# Revit family: ALBA_R100ExSWxxS
name_source: partatom
category: Leuchten
units: mm (PartAtom-declared; Revit-internal decimal feet)

## family parameters
Basisbauteil = Fläche
Beim Laden mit Abzugskörper schneiden = Nein
Bemaßung runder Anschluss = Durchmesser verwenden
Gemeinsam genutzt = Nein
Lichtquelle = Ja
OmniClass-Nummer = 23.80.70.11
OmniClass-Titel = Luminaries for Internal Lighting
Raumberechnungspunkt = Nein
Teiletyp = Normal

## types (8) — shared parameters
Baugruppenkennzeichen = D5020200
Datei für fotometrisches Netz = Master_ALBA_R100E_SW_Linse_S.IES
Emissionsform beim Rendern sichtbar = Nein
Farbfilter = 16777215
Farbtemperaturverschiebung bei Dämpfen der Lampe = <Keine Auswahl>
Hersteller = RIDI Leuchten GmbH
Lampe = LED
Neigungswinkel = 90.00°
Scheinlast = 15 VA
URL = www.ridi.de
Von Kreisdurchmesser aussenden = 86 mm  [stored 0.282152 ft]
brand = RIDI
conformity mark = CE
electrical safety class = 2
height = 84 mm  [stored 0.275591 ft]
ingress protection (IP) code = IP20
length = 112 mm  [stored 0.367454 ft]
nominal frequency = 50-60Hz
nominal voltage = 230
rated input power = 15
voltage type (AC, DC, UC) = AC
weight = 0.43 kg
width = 112 mm  [stored 0.367454 ft]
zero-valued in all types: Vorgabe-Ansicht

## per-type parameters (varying)
| type | Modell |
| ALBA R100E NDSW840S0200 | 0322319 |
| ALBA R100E NDSW830S0200 | 0322318 |
| ALBA R100E NDSW930S0175 | 0322320 |
| ALBA R100E NDSW940S0175 | 0322321 |
| ALBA R100E DASW830S0200 | 0332318 |
| ALBA R100E DASW840S0200 | 0332319 |
| ALBA R100E DASW930S0175 | 0332320 |
| ALBA R100E DASW940S0175 | 0332321 |

note: column(s) folded — value = type name in every type: product name

note: [stored X ft] marks values corroborated as IEEE doubles in the binary element streams (Revit-internal decimal feet)
